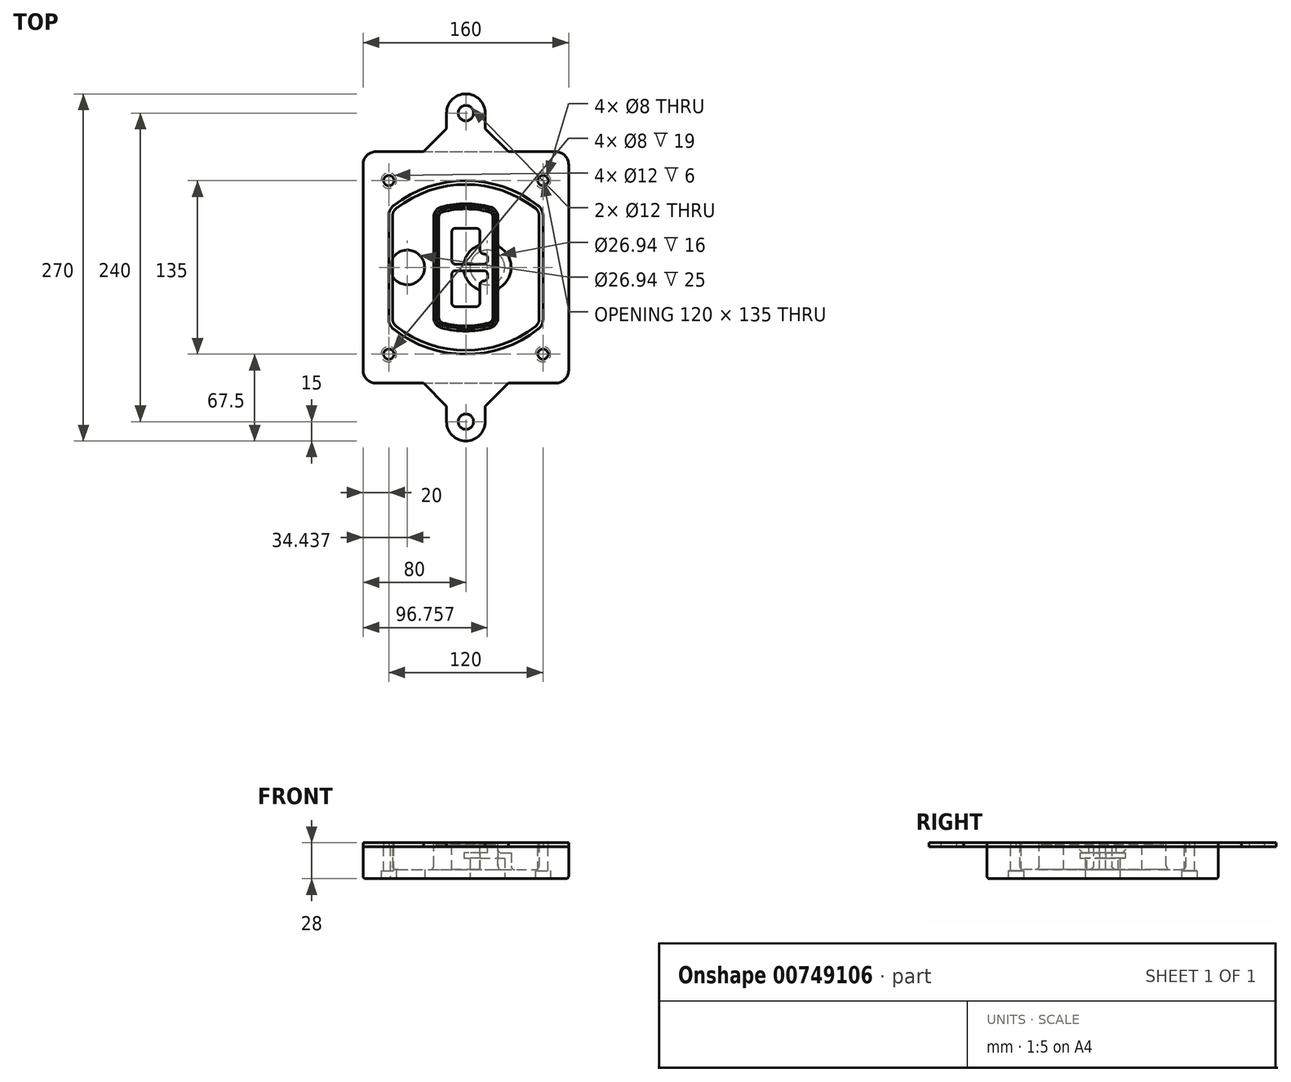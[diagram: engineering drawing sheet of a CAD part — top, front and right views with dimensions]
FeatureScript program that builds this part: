
annotation { "Feature Type Name" : "Feature", "Feature Type Description" : "" }
export const myFeature = defineFeature(function(context is Context, id is Id, definition is map)
    precondition{}
    {
        {
            var Q0;
            Q0=qCreatedBy(makeId("Top.planeOp"),FACE);
            var sketch = newSketch(context, id + "F0", { "sketchPlane" : qUnion([Q0])});
            skPoint(sketch, "E0.rect.middle", {"position": v(0, 0) * mm});
            skLineSegment(sketch, "E1.bottom", {"start": v(-70, -90) * mm, "end": v(70, -90) * mm});
            skLineSegment(sketch, "E1.top", {"start": v(-70, 90) * mm, "end": v(70, 90) * mm});
            skLineSegment(sketch, "E1.left", {"start": v(-80, -80) * mm, "end": v(-80, 80) * mm});
            skLineSegment(sketch, "E1.right", {"start": v(80, -80) * mm, "end": v(80, 80) * mm});
            skLineSegment(sketch, "E2", {"start": v(-80, 90) * mm, "end": v(80, -90) * mm, "construction": true});
            skLineSegment(sketch, "E3", {"start": v(80, 90) * mm, "end": v(-80, -90) * mm, "construction": true});
            skCircle(sketch, "E4", {"center": v(-60, 67.5) * mm, "radius": 4 * mm});
            skCircle(sketch, "E5", {"center": v(60, 67.5) * mm, "radius": 4 * mm});
            skCircle(sketch, "E6", {"center": v(60, -67.5) * mm, "radius": 4 * mm});
            skCircle(sketch, "E7", {"center": v(-60, -67.5) * mm, "radius": 4 * mm});
            skLineSegment(sketch, "E8", {"start": v(-60, 67.5) * mm, "end": v(60, 67.5) * mm, "construction": true});
            skLineSegment(sketch, "E9", {"start": v(60, 67.5) * mm, "end": v(60, -67.5) * mm, "construction": true});
            skLineSegment(sketch, "E10", {"start": v(60, -67.5) * mm, "end": v(-60, -67.5) * mm, "construction": true});
            skLineSegment(sketch, "E11", {"start": v(-60, -67.5) * mm, "end": v(-60, 67.5) * mm, "construction": true});
            skLineSegment(sketch, "E12", {"start": v(-60, 40.3) * mm, "end": v(-60, -40.3) * mm});
            skLineSegment(sketch, "E13", {"start": v(60, 40.3) * mm, "end": v(60, -40.3) * mm});
            skArc(sketch, "E14", {"start": v(56.15, 48.18) * mm, "mid": v(0, 67.5) * mm, "end": v(-56.15, 48.18) * mm});
            skArc(sketch, "E15", {"start": v(-56.15, -48.18) * mm, "mid": v(0, -67.5) * mm, "end": v(56.15, -48.18) * mm});
            skLineSegment(sketch, "E16", {"start": v(-60, 0) * mm, "end": v(60, 0) * mm, "construction": true});
            skPoint(sketch, "E17.visualSharp", {"position": v(-60, -45) * mm});
            skArc(sketch, "E17.filletArc", {"start": v(-60, -40.3) * mm, "mid": v(-58.99, -44.68) * mm, "end": v(-56.15, -48.18) * mm});
            skPoint(sketch, "E18.visualSharp", {"position": v(-60, 45) * mm});
            skArc(sketch, "E18.filletArc", {"start": v(-56.15, 48.18) * mm, "mid": v(-58.99, 44.68) * mm, "end": v(-60, 40.3) * mm});
            skPoint(sketch, "E19.visualSharp", {"position": v(60, 45) * mm});
            skArc(sketch, "E19.filletArc", {"start": v(60, 40.3) * mm, "mid": v(58.99, 44.68) * mm, "end": v(56.15, 48.18) * mm});
            skPoint(sketch, "E20.visualSharp", {"position": v(60, -45) * mm});
            skArc(sketch, "E20.filletArc", {"start": v(56.15, -48.18) * mm, "mid": v(58.99, -44.68) * mm, "end": v(60, -40.3) * mm});
            skPoint(sketch, "E21.visualSharp", {"position": v(-80, 90) * mm});
            skArc(sketch, "E21.filletArc", {"start": v(-70, 90) * mm, "mid": v(-77.07, 87.07) * mm, "end": v(-80, 80) * mm});
            skPoint(sketch, "E22.visualSharp", {"position": v(80, 90) * mm});
            skArc(sketch, "E22.filletArc", {"start": v(80, 80) * mm, "mid": v(77.07, 87.07) * mm, "end": v(70, 90) * mm});
            skPoint(sketch, "E23.visualSharp", {"position": v(80, -90) * mm});
            skArc(sketch, "E23.filletArc", {"start": v(70, -90) * mm, "mid": v(77.07, -87.07) * mm, "end": v(80, -80) * mm});
            skPoint(sketch, "E24.visualSharp", {"position": v(-80, -90) * mm});
            skArc(sketch, "E24.filletArc", {"start": v(-80, -80) * mm, "mid": v(-77.07, -87.07) * mm, "end": v(-70, -90) * mm});
            skArc(sketch, "E25.0", {"start": v(57, 40.3) * mm, "mid": v(56.3, 43.36) * mm, "end": v(54.3, 45.81) * mm});
            skLineSegment(sketch, "E25.1", {"start": v(57, 40.3) * mm, "end": v(57, -40.3) * mm});
            skArc(sketch, "E25.2", {"start": v(54.3, -45.81) * mm, "mid": v(56.3, -43.36) * mm, "end": v(57, -40.3) * mm});
            skArc(sketch, "E25.3", {"start": v(-54.3, -45.81) * mm, "mid": v(0, -64.5) * mm, "end": v(54.3, -45.81) * mm});
            skArc(sketch, "E25.4", {"start": v(-57, -40.3) * mm, "mid": v(-56.3, -43.36) * mm, "end": v(-54.3, -45.81) * mm});
            skArc(sketch, "E25.5", {"start": v(54.3, 45.81) * mm, "mid": v(0, 64.5) * mm, "end": v(-54.3, 45.81) * mm});
            skLineSegment(sketch, "E25.6", {"start": v(-57, 40.3) * mm, "end": v(-57, -40.3) * mm});
            skArc(sketch, "E25.7", {"start": v(-54.3, 45.81) * mm, "mid": v(-56.3, 43.36) * mm, "end": v(-57, 40.3) * mm});
            skArc(sketch, "E26.0", {"start": v(-58.62, 51.33) * mm, "mid": v(-62.58, 46.43) * mm, "end": v(-64, 40.3) * mm});
            skArc(sketch, "E26.1", {"start": v(58.62, 51.33) * mm, "mid": v(0, 71.5) * mm, "end": v(-58.62, 51.33) * mm});
            skArc(sketch, "E26.2", {"start": v(64, 40.3) * mm, "mid": v(62.58, 46.43) * mm, "end": v(58.62, 51.33) * mm});
            skLineSegment(sketch, "E26.3", {"start": v(64, 40.3) * mm, "end": v(64, -40.3) * mm});
            skArc(sketch, "E26.4", {"start": v(58.62, -51.33) * mm, "mid": v(62.58, -46.43) * mm, "end": v(64, -40.3) * mm});
            skLineSegment(sketch, "E26.5", {"start": v(-64, 40.3) * mm, "end": v(-64, -40.3) * mm});
            skArc(sketch, "E26.6", {"start": v(-58.62, -51.33) * mm, "mid": v(0, -71.5) * mm, "end": v(58.62, -51.33) * mm});
            skArc(sketch, "E26.7", {"start": v(-64, -40.3) * mm, "mid": v(-62.58, -46.43) * mm, "end": v(-58.62, -51.33) * mm});
            skSolve(sketch);
        }
        {
            var Q0;
            Q0=makeQuery(id+"F0.imprint","IMPRINT",FACE,{"disambiguationData":[TD([[makeQuery(id+"F0.imprint","IMPRINT",EDGE,{"derivedFrom":sQuery(id+"F0.wireOp",EDGE,"E1.bottom")}),1.0]])]});
            var Q1;
            Q1=makeQuery(id+"F0.imprint","IMPRINT",FACE,{"disambiguationData":[TD([[makeQuery(id+"F0.imprint","IMPRINT",EDGE,{"derivedFrom":sQuery(id+"F0.wireOp",EDGE,"E12")}),1.0]])]});
            var Q2;
            Q2=makeQuery(id+"F0.imprint","IMPRINT",FACE,{"disambiguationData":[TD([[makeQuery(id+"F0.imprint","IMPRINT",EDGE,{"derivedFrom":sQuery(id+"F0.wireOp",EDGE,"E25.0")}),1.0]])]});
            var Q3;
            Q3=makeQuery(id+"F0.imprint","IMPRINT",FACE,{"disambiguationData":[TD([[makeQuery(id+"F0.imprint","IMPRINT",EDGE,{"derivedFrom":sQuery(id+"F0.wireOp",EDGE,"E12")}),-1.0]])]});
            extrude(context, id + "F1", {"entities" : qUnion([Q0, Q1, Q2, Q3]), "oppositeDirection" : true, "depth" : 25 * mm});
        }
        {
            var Q0;
            Q0=makeQuery(id+"F0.imprint","IMPRINT",FACE,{"disambiguationData":[TD([[makeQuery(id+"F0.imprint","IMPRINT",EDGE,{"derivedFrom":sQuery(id+"F0.wireOp",EDGE,"E12")}),1.0]])]});
            extrude(context, id + "F2", {"entities" : qUnion([Q0]), "operationType" : NewBodyOperationType.ADD, "depth" : 3 * mm});
        }
        {
            var Q0;
            Q0=makeQuery(id+"F0.imprint","IMPRINT",FACE,{"disambiguationData":[TD([[makeQuery(id+"F0.imprint","IMPRINT",EDGE,{"derivedFrom":sQuery(id+"F0.wireOp",EDGE,"E25.0")}),1.0]])]});
            extrude(context, id + "F3", {"entities" : qUnion([Q0]), "operationType" : NewBodyOperationType.REMOVE, "oppositeDirection" : true, "depth" : 18 * mm});
        }
        {
            var Q0;
            Q0=makeQuery(id+"F2.opExtrude","CAP_FACE",FACE,{"disambiguationData":[OSD([sQuery(id+"F0.wireOp",EDGE,"E12"),sQuery(id+"F0.wireOp",EDGE,"E13"),sQuery(id+"F0.wireOp",EDGE,"E14"),sQuery(id+"F0.wireOp",EDGE,"E15"),sQuery(id+"F0.wireOp",EDGE,"E17.filletArc"),sQuery(id+"F0.wireOp",EDGE,"E18.filletArc"),sQuery(id+"F0.wireOp",EDGE,"E19.filletArc"),sQuery(id+"F0.wireOp",EDGE,"E20.filletArc"),sQuery(id+"F0.wireOp",EDGE,"E25.0"),sQuery(id+"F0.wireOp",EDGE,"E25.1"),sQuery(id+"F0.wireOp",EDGE,"E25.2"),sQuery(id+"F0.wireOp",EDGE,"E25.3"),sQuery(id+"F0.wireOp",EDGE,"E25.4"),sQuery(id+"F0.wireOp",EDGE,"E25.5"),sQuery(id+"F0.wireOp",EDGE,"E25.6"),sQuery(id+"F0.wireOp",EDGE,"E25.7")])],"isStart":false});
            var sketch = newSketch(context, id + "F4", { "sketchPlane" : qUnion([Q0])});
            skArc(sketch, "E27.0", {"start": v(-19.08, -46.97) * mm, "mid": v(0, -49.5) * mm, "end": v(19.08, -46.97) * mm});
            skArc(sketch, "E28.0", {"start": v(19.08, 46.97) * mm, "mid": v(0, 49.5) * mm, "end": v(-19.08, 46.97) * mm});
            skLineSegment(sketch, "E29", {"start": v(-25, 39.25) * mm, "end": v(-25, -39.25) * mm});
            skLineSegment(sketch, "E30", {"start": v(25, 39.25) * mm, "end": v(25, -39.25) * mm});
            skLineSegment(sketch, "E31", {"start": v(-25, 45.1) * mm, "end": v(25, 45.1) * mm, "construction": true});
            skLineSegment(sketch, "E32", {"start": v(-25, -45.1) * mm, "end": v(25, -45.1) * mm, "construction": true});
            skPoint(sketch, "E33.visualSharp", {"position": v(-25, 45.1) * mm});
            skArc(sketch, "E33.filletArc", {"start": v(-19.08, 46.97) * mm, "mid": v(-23.35, 44.11) * mm, "end": v(-25, 39.25) * mm});
            skPoint(sketch, "E34.visualSharp", {"position": v(25, 45.1) * mm});
            skArc(sketch, "E34.filletArc", {"start": v(25, 39.25) * mm, "mid": v(23.35, 44.11) * mm, "end": v(19.08, 46.97) * mm});
            skPoint(sketch, "E35.visualSharp", {"position": v(25, -45.1) * mm});
            skArc(sketch, "E35.filletArc", {"start": v(19.08, -46.97) * mm, "mid": v(23.35, -44.11) * mm, "end": v(25, -39.25) * mm});
            skPoint(sketch, "E36.visualSharp", {"position": v(-25, -45.1) * mm});
            skArc(sketch, "E36.filletArc", {"start": v(-25, -39.25) * mm, "mid": v(-23.35, -44.11) * mm, "end": v(-19.08, -46.97) * mm});
            skArc(sketch, "E37.0", {"start": v(54.3, 45.81) * mm, "mid": v(0, 64.5) * mm, "end": v(-54.3, 45.81) * mm});
            skArc(sketch, "E37.1", {"start": v(-54.3, 45.81) * mm, "mid": v(-56.3, 43.36) * mm, "end": v(-57, 40.3) * mm});
            skLineSegment(sketch, "E37.2", {"start": v(-57, 40.3) * mm, "end": v(-57, -40.3) * mm});
            skArc(sketch, "E37.3", {"start": v(-57, -40.3) * mm, "mid": v(-56.3, -43.36) * mm, "end": v(-54.3, -45.81) * mm});
            skArc(sketch, "E37.4", {"start": v(-54.3, -45.81) * mm, "mid": v(0, -64.5) * mm, "end": v(54.3, -45.81) * mm});
            skArc(sketch, "E37.5", {"start": v(54.3, -45.81) * mm, "mid": v(56.3, -43.36) * mm, "end": v(57, -40.3) * mm});
            skLineSegment(sketch, "E37.6", {"start": v(57, 40.3) * mm, "end": v(57, -40.3) * mm});
            skArc(sketch, "E37.7", {"start": v(57, 40.3) * mm, "mid": v(56.3, 43.36) * mm, "end": v(54.3, 45.81) * mm});
            skLineSegment(sketch, "E38.0", {"start": v(23, 39.25) * mm, "end": v(23, -39.25) * mm});
            skArc(sketch, "E38.1", {"start": v(18.56, -45.04) * mm, "mid": v(21.76, -42.9) * mm, "end": v(23, -39.25) * mm});
            skArc(sketch, "E38.2", {"start": v(-18.56, -45.04) * mm, "mid": v(0, -47.5) * mm, "end": v(18.56, -45.04) * mm});
            skArc(sketch, "E38.3", {"start": v(-23, -39.25) * mm, "mid": v(-21.76, -42.9) * mm, "end": v(-18.56, -45.04) * mm});
            skLineSegment(sketch, "E38.4", {"start": v(-23, 39.25) * mm, "end": v(-23, -39.25) * mm});
            skArc(sketch, "E38.5", {"start": v(23, 39.25) * mm, "mid": v(21.76, 42.9) * mm, "end": v(18.56, 45.04) * mm});
            skArc(sketch, "E38.6", {"start": v(-18.56, 45.04) * mm, "mid": v(-21.76, 42.9) * mm, "end": v(-23, 39.25) * mm});
            skArc(sketch, "E38.7", {"start": v(18.56, 45.04) * mm, "mid": v(0, 47.5) * mm, "end": v(-18.56, 45.04) * mm});
            skArc(sketch, "E39.0", {"start": v(21, 39.25) * mm, "mid": v(20.18, 41.68) * mm, "end": v(18.04, 43.1) * mm});
            skLineSegment(sketch, "E39.1", {"start": v(21, 39.25) * mm, "end": v(21, -39.25) * mm});
            skArc(sketch, "E39.2", {"start": v(18.04, -43.1) * mm, "mid": v(20.18, -41.68) * mm, "end": v(21, -39.25) * mm});
            skArc(sketch, "E39.3", {"start": v(-18.04, -43.1) * mm, "mid": v(0, -45.5) * mm, "end": v(18.04, -43.1) * mm});
            skArc(sketch, "E39.4", {"start": v(-21, -39.25) * mm, "mid": v(-20.18, -41.68) * mm, "end": v(-18.04, -43.1) * mm});
            skArc(sketch, "E39.5", {"start": v(18.04, 43.1) * mm, "mid": v(0, 45.5) * mm, "end": v(-18.04, 43.1) * mm});
            skLineSegment(sketch, "E39.6", {"start": v(-21, 39.25) * mm, "end": v(-21, -39.25) * mm});
            skArc(sketch, "E39.7", {"start": v(-18.04, 43.1) * mm, "mid": v(-20.18, 41.68) * mm, "end": v(-21, 39.25) * mm});
            skLineSegment(sketch, "E40", {"start": v(-25, 0) * mm, "end": v(25, 0) * mm, "construction": true});
            skLineSegment(sketch, "E41", {"start": v(-11, 5.5) * mm, "end": v(-11, 27.5) * mm});
            skLineSegment(sketch, "E42", {"start": v(-8, 30.5) * mm, "end": v(8, 30.5) * mm});
            skLineSegment(sketch, "E43", {"start": v(11, 27.5) * mm, "end": v(11, 13.5) * mm});
            skLineSegment(sketch, "E44", {"start": v(14, 10.5) * mm, "end": v(14, 10.5) * mm});
            skLineSegment(sketch, "E45", {"start": v(17, 7.5) * mm, "end": v(17, 5.5) * mm});
            skLineSegment(sketch, "E46", {"start": v(14, 2.5) * mm, "end": v(-8, 2.5) * mm});
            skPoint(sketch, "E47.visualSharp", {"position": v(-11, 30.5) * mm});
            skArc(sketch, "E47.filletArc", {"start": v(-8, 30.5) * mm, "mid": v(-10.12, 29.62) * mm, "end": v(-11, 27.5) * mm});
            skPoint(sketch, "E48.visualSharp", {"position": v(11, 30.5) * mm});
            skArc(sketch, "E48.filletArc", {"start": v(11, 27.5) * mm, "mid": v(10.12, 29.62) * mm, "end": v(8, 30.5) * mm});
            skPoint(sketch, "E49.visualSharp", {"position": v(11, 10.5) * mm});
            skArc(sketch, "E49.filletArc", {"start": v(11, 13.5) * mm, "mid": v(11.88, 11.38) * mm, "end": v(14, 10.5) * mm});
            skPoint(sketch, "E50.visualSharp", {"position": v(17, 10.5) * mm});
            skArc(sketch, "E50.filletArc", {"start": v(17, 7.5) * mm, "mid": v(16.12, 9.62) * mm, "end": v(14, 10.5) * mm});
            skPoint(sketch, "E51.visualSharp", {"position": v(17, 2.5) * mm});
            skArc(sketch, "E51.filletArc", {"start": v(14, 2.5) * mm, "mid": v(16.12, 3.38) * mm, "end": v(17, 5.5) * mm});
            skPoint(sketch, "E52.visualSharp", {"position": v(-11, 2.5) * mm});
            skArc(sketch, "E52.filletArc", {"start": v(-11, 5.5) * mm, "mid": v(-10.12, 3.38) * mm, "end": v(-8, 2.5) * mm});
            skLineSegment(sketch, "E53.0.MirrorCS", {"start": v(14, -2.5) * mm, "end": v(-8, -2.5) * mm});
            skArc(sketch, "E54.0.MirrorCS", {"start": v(-11, -5.5) * mm, "mid": v(-10.12, -3.38) * mm, "end": v(-8, -2.5) * mm});
            skLineSegment(sketch, "E55.0.MirrorCS", {"start": v(-11, -5.5) * mm, "end": v(-11, -27.5) * mm});
            skArc(sketch, "E56.0.MirrorCS", {"start": v(-8, -30.5) * mm, "mid": v(-10.12, -29.62) * mm, "end": v(-11, -27.5) * mm});
            skLineSegment(sketch, "E57.0.MirrorCS", {"start": v(-8, -30.5) * mm, "end": v(8, -30.5) * mm});
            skArc(sketch, "E58.0.MirrorCS", {"start": v(11, -27.5) * mm, "mid": v(10.12, -29.62) * mm, "end": v(8, -30.5) * mm});
            skLineSegment(sketch, "E59.0.MirrorCS", {"start": v(11, -27.5) * mm, "end": v(11, -13.5) * mm});
            skArc(sketch, "E60.0.MirrorCS", {"start": v(11, -13.5) * mm, "mid": v(11.88, -11.38) * mm, "end": v(14, -10.5) * mm});
            skArc(sketch, "E61.0.MirrorCS", {"start": v(17, -7.5) * mm, "mid": v(16.12, -9.62) * mm, "end": v(14, -10.5) * mm});
            skLineSegment(sketch, "E62.0.MirrorCS", {"start": v(17, -7.5) * mm, "end": v(17, -5.5) * mm});
            skArc(sketch, "E63.0.MirrorCS", {"start": v(14, -2.5) * mm, "mid": v(16.12, -3.38) * mm, "end": v(17, -5.5) * mm});
            skSolve(sketch);
        }
        {
            var Q0;
            Q0=makeQuery(id+"F4.imprint","IMPRINT",FACE,{"disambiguationData":[TD([[makeQuery(id+"F4.imprint","IMPRINT",EDGE,{"derivedFrom":sQuery(id+"F4.wireOp",EDGE,"E27.0")}),1.0]])]});
            var Q1;
            Q1=makeQuery(id+"F4.imprint","IMPRINT",FACE,{"disambiguationData":[TD([[makeQuery(id+"F4.imprint","IMPRINT",EDGE,{"derivedFrom":sQuery(id+"F4.wireOp",EDGE,"E38.0")}),-1.0]])]});
            var Q2;
            Q2=makeQuery(id+"F4.imprint","IMPRINT",FACE,{"disambiguationData":[TD([[makeQuery(id+"F4.imprint","IMPRINT",EDGE,{"derivedFrom":sQuery(id+"F4.wireOp",EDGE,"E39.0")}),1.0]])]});
            extrude(context, id + "F5", {"entities" : qUnion([Q0, Q1, Q2]), "operationType" : NewBodyOperationType.ADD, "endBound" : BoundingType.UP_TO_NEXT, "oppositeDirection" : true, "depth" : 25 * mm});
        }
        {
            var Q0;
            Q0=makeQuery(id+"F4.imprint","IMPRINT",FACE,{"disambiguationData":[TD([[makeQuery(id+"F4.imprint","IMPRINT",EDGE,{"derivedFrom":sQuery(id+"F4.wireOp",EDGE,"E38.0")}),-1.0]])]});
            extrude(context, id + "F6", {"entities" : qUnion([Q0]), "operationType" : NewBodyOperationType.REMOVE, "oppositeDirection" : true, "depth" : 2 * mm});
        }
        {
            var Q0;
            Q0=makeQuery(id+"F1.opExtrude","CAP_FACE",FACE,{"disambiguationData":[OSD([sQuery(id+"F0.wireOp",EDGE,"E1.bottom"),sQuery(id+"F0.wireOp",EDGE,"E1.top"),sQuery(id+"F0.wireOp",EDGE,"E1.left"),sQuery(id+"F0.wireOp",EDGE,"E1.right"),sQuery(id+"F0.wireOp",EDGE,"E4"),sQuery(id+"F0.wireOp",EDGE,"E5"),sQuery(id+"F0.wireOp",EDGE,"E6"),sQuery(id+"F0.wireOp",EDGE,"E7"),sQuery(id+"F0.wireOp",EDGE,"E21.filletArc"),sQuery(id+"F0.wireOp",EDGE,"E22.filletArc"),sQuery(id+"F0.wireOp",EDGE,"E23.filletArc"),sQuery(id+"F0.wireOp",EDGE,"E24.filletArc")])],"isStart":false});
            var sketch = newSketch(context, id + "F7", { "sketchPlane" : qUnion([Q0])});
            skCircle(sketch, "E64", {"center": v(16.76, 0) * mm, "radius": 13.47 * mm});
            skCircle(sketch, "E65", {"center": v(-45.56, 0) * mm, "radius": 13.47 * mm});
            skLineSegment(sketch, "E66", {"start": v(80, 0) * mm, "end": v(-80, 0) * mm});
            skCircle(sketch, "E67", {"center": v(16.76, 0) * mm, "radius": 18.47 * mm});
            skCircle(sketch, "E68", {"center": v(60, -67.5) * mm, "radius": 6 * mm});
            skCircle(sketch, "E69", {"center": v(-60, -67.5) * mm, "radius": 6 * mm});
            skCircle(sketch, "E70", {"center": v(-60, 67.5) * mm, "radius": 6 * mm});
            skCircle(sketch, "E71", {"center": v(60, 67.5) * mm, "radius": 6 * mm});
            skSolve(sketch);
        }
        {
            var Q0;
            {var subQ1=sQuery(id+"F7.wireOp",EDGE,"E66");var subQ4=sQuery(id+"F7.wireOp",EDGE,"E64");var subQ6=makeQuery(id+"F7.imprint","INTERSECT",VERTEX,{"disambiguationData":[OD(0.0)],"derivedFrom":[subQ4,subQ1]});Q0=makeQuery(id+"F7.imprint","IMPRINT",FACE,{"disambiguationData":[TD([[makeQuery(id+"F7.imprint","IMPRINT",EDGE,{"disambiguationData":[TD([[subQ6,-1.0]])],"derivedFrom":subQ4}),-1.0]])]});}
            var Q1;
            {var subQ0=sQuery(id+"F7.wireOp",EDGE,"E66");var subQ1=sQuery(id+"F7.wireOp",EDGE,"E64");var subQ3=makeQuery(id+"F7.imprint","INTERSECT",VERTEX,{"disambiguationData":[OD(0.0)],"derivedFrom":[subQ1,subQ0]});Q1=makeQuery(id+"F7.imprint","IMPRINT",FACE,{"disambiguationData":[TD([[makeQuery(id+"F7.imprint","IMPRINT",EDGE,{"disambiguationData":[TD([[subQ3,-1.0]])],"derivedFrom":subQ1}),1.0]])]});}
            var Q2;
            {var subQ0=sQuery(id+"F7.wireOp",EDGE,"E66");var subQ1=sQuery(id+"F7.wireOp",EDGE,"E64");var subQ3=makeQuery(id+"F7.imprint","INTERSECT",VERTEX,{"disambiguationData":[OD(0.0)],"derivedFrom":[subQ1,subQ0]});Q2=makeQuery(id+"F7.imprint","IMPRINT",FACE,{"disambiguationData":[TD([[makeQuery(id+"F7.imprint","IMPRINT",EDGE,{"disambiguationData":[TD([[subQ3,1.0]])],"derivedFrom":subQ1}),1.0]])]});}
            var Q3;
            {var subQ1=sQuery(id+"F7.wireOp",EDGE,"E66");var subQ4=sQuery(id+"F7.wireOp",EDGE,"E64");var subQ6=makeQuery(id+"F7.imprint","INTERSECT",VERTEX,{"disambiguationData":[OD(0.0)],"derivedFrom":[subQ4,subQ1]});Q3=makeQuery(id+"F7.imprint","IMPRINT",FACE,{"disambiguationData":[TD([[makeQuery(id+"F7.imprint","IMPRINT",EDGE,{"disambiguationData":[TD([[subQ6,1.0]])],"derivedFrom":subQ4}),-1.0]])]});}
            extrude(context, id + "F8", {"entities" : qUnion([Q0, Q1, Q2, Q3]), "operationType" : NewBodyOperationType.ADD, "oppositeDirection" : true, "depth" : 20 * mm});
        }
        {
            var Q0;
            {var subQ0=sQuery(id+"F7.wireOp",EDGE,"E66");var subQ1=sQuery(id+"F7.wireOp",EDGE,"E64");var subQ3=makeQuery(id+"F7.imprint","INTERSECT",VERTEX,{"disambiguationData":[OD(0.0)],"derivedFrom":[subQ1,subQ0]});Q0=makeQuery(id+"F7.imprint","IMPRINT",FACE,{"disambiguationData":[TD([[makeQuery(id+"F7.imprint","IMPRINT",EDGE,{"disambiguationData":[TD([[subQ3,-1.0]])],"derivedFrom":subQ1}),1.0]])]});}
            var Q1;
            {var subQ0=sQuery(id+"F7.wireOp",EDGE,"E66");var subQ1=sQuery(id+"F7.wireOp",EDGE,"E64");var subQ3=makeQuery(id+"F7.imprint","INTERSECT",VERTEX,{"disambiguationData":[OD(0.0)],"derivedFrom":[subQ1,subQ0]});Q1=makeQuery(id+"F7.imprint","IMPRINT",FACE,{"disambiguationData":[TD([[makeQuery(id+"F7.imprint","IMPRINT",EDGE,{"disambiguationData":[TD([[subQ3,1.0]])],"derivedFrom":subQ1}),1.0]])]});}
            extrude(context, id + "F9", {"entities" : qUnion([Q0, Q1]), "operationType" : NewBodyOperationType.REMOVE, "oppositeDirection" : true, "depth" : 16 * mm});
        }
        {
            var Q0;
            {var subQ0=sQuery(id+"F7.wireOp",EDGE,"E66");var subQ1=sQuery(id+"F7.wireOp",EDGE,"E65");var subQ3=makeQuery(id+"F7.imprint","INTERSECT",VERTEX,{"disambiguationData":[OD(0.0)],"derivedFrom":[subQ1,subQ0]});Q0=makeQuery(id+"F7.imprint","IMPRINT",FACE,{"disambiguationData":[TD([[makeQuery(id+"F7.imprint","IMPRINT",EDGE,{"disambiguationData":[TD([[subQ3,-1.0]])],"derivedFrom":subQ1}),1.0]])]});}
            var Q1;
            {var subQ0=sQuery(id+"F7.wireOp",EDGE,"E66");var subQ1=sQuery(id+"F7.wireOp",EDGE,"E65");var subQ3=makeQuery(id+"F7.imprint","INTERSECT",VERTEX,{"disambiguationData":[OD(0.0)],"derivedFrom":[subQ1,subQ0]});Q1=makeQuery(id+"F7.imprint","IMPRINT",FACE,{"disambiguationData":[TD([[makeQuery(id+"F7.imprint","IMPRINT",EDGE,{"disambiguationData":[TD([[subQ3,1.0]])],"derivedFrom":subQ1}),1.0]])]});}
            extrude(context, id + "F10", {"entities" : qUnion([Q0, Q1]), "operationType" : NewBodyOperationType.REMOVE, "oppositeDirection" : true, "depth" : 25 * mm});
        }
        {
            var Q0;
            Q0=makeQuery(id+"F7.imprint","IMPRINT",FACE,{"disambiguationData":[TD([[makeQuery(id+"F7.imprint","IMPRINT",EDGE,{"derivedFrom":sQuery(id+"F7.wireOp",EDGE,"E68")}),1.0]])]});
            var Q1;
            Q1=makeQuery(id+"F7.imprint","IMPRINT",FACE,{"disambiguationData":[TD([[makeQuery(id+"F7.imprint","IMPRINT",EDGE,{"derivedFrom":makeQuery(id+"F1.opExtrude","CAP_EDGE",EDGE,{"disambiguationData":[OSD([sQuery(id+"F0.wireOp",EDGE,"E5")])],"isStart":false})}),-1.0]])]});
            var Q2;
            Q2=makeQuery(id+"F7.imprint","IMPRINT",FACE,{"disambiguationData":[TD([[makeQuery(id+"F7.imprint","IMPRINT",EDGE,{"derivedFrom":sQuery(id+"F7.wireOp",EDGE,"E69")}),1.0]])]});
            var Q3;
            Q3=makeQuery(id+"F7.imprint","IMPRINT",FACE,{"disambiguationData":[TD([[makeQuery(id+"F7.imprint","IMPRINT",EDGE,{"derivedFrom":makeQuery(id+"F1.opExtrude","CAP_EDGE",EDGE,{"disambiguationData":[OSD([sQuery(id+"F0.wireOp",EDGE,"E4")])],"isStart":false})}),-1.0]])]});
            var Q4;
            Q4=makeQuery(id+"F7.imprint","IMPRINT",FACE,{"disambiguationData":[TD([[makeQuery(id+"F7.imprint","IMPRINT",EDGE,{"derivedFrom":sQuery(id+"F7.wireOp",EDGE,"E70")}),1.0]])]});
            var Q5;
            Q5=makeQuery(id+"F7.imprint","IMPRINT",FACE,{"disambiguationData":[TD([[makeQuery(id+"F7.imprint","IMPRINT",EDGE,{"derivedFrom":makeQuery(id+"F1.opExtrude","CAP_EDGE",EDGE,{"disambiguationData":[OSD([sQuery(id+"F0.wireOp",EDGE,"E7")])],"isStart":false})}),-1.0]])]});
            var Q6;
            Q6=makeQuery(id+"F7.imprint","IMPRINT",FACE,{"disambiguationData":[TD([[makeQuery(id+"F7.imprint","IMPRINT",EDGE,{"derivedFrom":sQuery(id+"F7.wireOp",EDGE,"E71")}),1.0]])]});
            var Q7;
            Q7=makeQuery(id+"F7.imprint","IMPRINT",FACE,{"disambiguationData":[TD([[makeQuery(id+"F7.imprint","IMPRINT",EDGE,{"derivedFrom":makeQuery(id+"F1.opExtrude","CAP_EDGE",EDGE,{"disambiguationData":[OSD([sQuery(id+"F0.wireOp",EDGE,"E6")])],"isStart":false})}),-1.0]])]});
            extrude(context, id + "F11", {"entities" : qUnion([Q0, Q1, Q2, Q3, Q4, Q5, Q6, Q7]), "operationType" : NewBodyOperationType.REMOVE, "oppositeDirection" : true, "depth" : 6 * mm});
        }
        {
            var Q0;
            Q0=makeQuery(id+"F9.boolean.opBoolean","COPY",FACE,{"derivedFrom":makeQuery(id+"F9.opExtrude","CAP_FACE",FACE,{"disambiguationData":[OSD([sQuery(id+"F7.wireOp",EDGE,"E64")])],"isStart":false})});
            var sketch = newSketch(context, id + "F12", { "sketchPlane" : qUnion([Q0])});
            skArc(sketch, "E72.0", {"start": v(11, 17.55) * mm, "mid": v(2.57, 11.82) * mm, "end": v(-1.54, 2.5) * mm});
            skArc(sketch, "E72.1", {"start": v(-1.54, -2.5) * mm, "mid": v(2.57, -11.82) * mm, "end": v(11, -17.55) * mm});
            skLineSegment(sketch, "E73", {"start": v(-1.54, -2.5) * mm, "end": v(14, -2.5) * mm});
            skLineSegment(sketch, "E74.0", {"start": v(14, 2.5) * mm, "end": v(-1.54, 2.5) * mm});
            skArc(sketch, "E74.1", {"start": v(14, 2.5) * mm, "mid": v(16.12, 3.38) * mm, "end": v(17, 5.5) * mm});
            skLineSegment(sketch, "E74.2", {"start": v(17, 7.5) * mm, "end": v(17, 5.5) * mm});
            skArc(sketch, "E74.3", {"start": v(17, 7.5) * mm, "mid": v(16.12, 9.62) * mm, "end": v(14, 10.5) * mm});
            skArc(sketch, "E74.4", {"start": v(11, 13.5) * mm, "mid": v(11.88, 11.38) * mm, "end": v(14, 10.5) * mm});
            skLineSegment(sketch, "E74.5", {"start": v(11, 17.55) * mm, "end": v(11, 13.5) * mm});
            skLineSegment(sketch, "E74.7", {"start": v(14, -2.5) * mm, "end": v(-1.54, -2.5) * mm});
            skArc(sketch, "E74.8", {"start": v(14, -2.5) * mm, "mid": v(16.12, -3.38) * mm, "end": v(17, -5.5) * mm});
            skLineSegment(sketch, "E74.9", {"start": v(17, -7.5) * mm, "end": v(17, -5.5) * mm});
            skArc(sketch, "E74.10", {"start": v(17, -7.5) * mm, "mid": v(16.12, -9.62) * mm, "end": v(14, -10.5) * mm});
            skArc(sketch, "E74.11", {"start": v(11, -13.5) * mm, "mid": v(11.88, -11.38) * mm, "end": v(14, -10.5) * mm});
            skLineSegment(sketch, "E74.12", {"start": v(11, -17.55) * mm, "end": v(11, -13.5) * mm});
            skPoint(sketch, "E75.orphan", {"position": v(11, -27.5) * mm});
            skPoint(sketch, "E76.orphan", {"position": v(-8, -2.5) * mm});
            skPoint(sketch, "E77.orphan", {"position": v(-8, 2.5) * mm});
            skPoint(sketch, "E78.orphan", {"position": v(11, 27.5) * mm});
            skSolve(sketch);
        }
        {
            var Q0;
            {var subQ7=sQuery(id+"F12.wireOp",EDGE,"E72.0");var subQ14=sQuery(id+"F12.wireOp",EDGE,"E72.1");var subQ16=sQuery(id+"F12.wireOp",EDGE,"E74.1");var subQ18=sQuery(id+"F12.wireOp",EDGE,"E74.8");Q0=qUnion([makeQuery(id+"F12.imprint","IMPRINT",FACE,{"disambiguationData":[TD([[makeQuery(id+"F12.imprint","IMPRINT",EDGE,{"derivedFrom":subQ7}),1.0]])]}),makeQuery(id+"F12.imprint","IMPRINT",FACE,{"disambiguationData":[TD([[makeQuery(id+"F12.imprint","IMPRINT",EDGE,{"derivedFrom":subQ14}),1.0]])]}),makeQuery(id+"F12.imprint","IMPRINT",FACE,{"disambiguationData":[TD([[makeQuery(id+"F12.imprint","IMPRINT",EDGE,{"derivedFrom":subQ16}),1.0]])]}),makeQuery(id+"F12.imprint","IMPRINT",FACE,{"disambiguationData":[TD([[makeQuery(id+"F12.imprint","IMPRINT",EDGE,{"derivedFrom":subQ18}),-1.0]])]})]);}
            var Q1;
            Q1=makeQuery(id+"F5.boolean.opBoolean","SPLIT",FACE,{"disambiguationData":[TD([makeQuery(id+"F5.opExtrude","SWEPT_FACE",FACE,{"disambiguationData":[OSD([sQuery(id+"F4.wireOp",EDGE,"E41")])]})])],"derivedFrom":makeQuery(id+"F3.boolean.opBoolean","COPY",FACE,{"derivedFrom":makeQuery(id+"F3.opExtrude","CAP_FACE",FACE,{"disambiguationData":[OSD([sQuery(id+"F0.wireOp",EDGE,"E25.0"),sQuery(id+"F0.wireOp",EDGE,"E25.1"),sQuery(id+"F0.wireOp",EDGE,"E25.2"),sQuery(id+"F0.wireOp",EDGE,"E25.3"),sQuery(id+"F0.wireOp",EDGE,"E25.4"),sQuery(id+"F0.wireOp",EDGE,"E25.5"),sQuery(id+"F0.wireOp",EDGE,"E25.6"),sQuery(id+"F0.wireOp",EDGE,"E25.7")])],"isStart":false})})});
            extrude(context, id + "F13", {"entities" : qUnion([Q0]), "operationType" : NewBodyOperationType.REMOVE, "endBound" : BoundingType.UP_TO_SURFACE, "endBoundEntityFace" : qUnion([Q1]), "depth" : 25 * mm});
        }
        {
            var Q0;
            Q0=makeQuery(id+"F3.boolean.opBoolean","COPY",EDGE,{"derivedFrom":makeQuery(id+"F3.opExtrude","CAP_EDGE",EDGE,{"disambiguationData":[OSD([sQuery(id+"F0.wireOp",EDGE,"E25.6")])],"isStart":false})});
            var Q1;
            Q1=makeQuery(id+"F8.boolean.opBoolean","INTERSECT",EDGE,{"derivedFrom":[makeQuery(id+"F5.opExtrude","SWEPT_FACE",FACE,{"disambiguationData":[OSD([sQuery(id+"F4.wireOp",EDGE,"E30")])]}),makeQuery(id+"F8.opExtrude","CAP_FACE",FACE,{"disambiguationData":[OSD([sQuery(id+"F7.wireOp",EDGE,"E67")])],"isStart":false})]});
            var Q2;
            Q2=makeQuery(id+"F8.boolean.opBoolean","INTERSECT",EDGE,{"disambiguationData":[OD(1.0)],"derivedFrom":[makeQuery(id+"F5.opExtrude","SWEPT_FACE",FACE,{"disambiguationData":[OSD([sQuery(id+"F4.wireOp",EDGE,"E30")])]}),makeQuery(id+"F8.opExtrude","SWEPT_FACE",FACE,{"disambiguationData":[OSD([sQuery(id+"F7.wireOp",EDGE,"E67")])]})]});
            var Q3;
            {var subQ0=sQuery(id+"F4.wireOp",EDGE,"E30");Q3=makeQuery(id+"F8.boolean.opBoolean","SPLIT",EDGE,{"disambiguationData":[TD([makeQuery(id+"F5.opExtrude","SWEPT_FACE",FACE,{"disambiguationData":[OSD([sQuery(id+"F4.wireOp",EDGE,"E35.filletArc")])]})])],"derivedFrom":makeQuery(id+"F5.opExtrude","CAP_EDGE",EDGE,{"disambiguationData":[OSD([subQ0])],"isStart":false})});}
            var Q4;
            {var subQ0=sQuery(id+"F0.wireOp",EDGE,"E25.7");var subQ1=sQuery(id+"F0.wireOp",EDGE,"E25.1");var subQ2=sQuery(id+"F0.wireOp",EDGE,"E25.6");var subQ3=sQuery(id+"F0.wireOp",EDGE,"E25.5");var subQ4=sQuery(id+"F0.wireOp",EDGE,"E25.4");var subQ5=sQuery(id+"F0.wireOp",EDGE,"E25.0");var subQ6=sQuery(id+"F0.wireOp",EDGE,"E25.2");var subQ7=sQuery(id+"F0.wireOp",EDGE,"E25.3");Q4=makeQuery(id+"F8.boolean.opBoolean","INTERSECT",EDGE,{"derivedFrom":[makeQuery(id+"F5.boolean.opBoolean","SPLIT",FACE,{"disambiguationData":[TD([makeQuery(id+"F2.opExtrude","SWEPT_FACE",FACE,{"disambiguationData":[OSD([subQ5])]})])],"derivedFrom":makeQuery(id+"F3.boolean.opBoolean","COPY",FACE,{"derivedFrom":makeQuery(id+"F3.opExtrude","CAP_FACE",FACE,{"disambiguationData":[OSD([subQ5,subQ1,subQ6,subQ7,subQ4,subQ3,subQ2,subQ0])],"isStart":false})})}),makeQuery(id+"F8.opExtrude","SWEPT_FACE",FACE,{"disambiguationData":[OSD([sQuery(id+"F7.wireOp",EDGE,"E67")])]})]});}
            var Q5;
            Q5=makeQuery(id+"F8.boolean.opBoolean","INTERSECT",EDGE,{"disambiguationData":[OD(0.0)],"derivedFrom":[makeQuery(id+"F5.opExtrude","SWEPT_FACE",FACE,{"disambiguationData":[OSD([sQuery(id+"F4.wireOp",EDGE,"E30")])]}),makeQuery(id+"F8.opExtrude","SWEPT_FACE",FACE,{"disambiguationData":[OSD([sQuery(id+"F7.wireOp",EDGE,"E67")])]})]});
            fillet(context, id + "F14", {"entities" : qUnion([Q0, Q1, Q2, Q3, Q4, Q5]), "radius" : 3 * mm, "tangentPropagation" : true, "allowEdgeOverflow" : false});
        }
        {
            var Q0;
            Q0=makeQuery(id+"F1.opExtrude","CAP_EDGE",EDGE,{"disambiguationData":[OSD([sQuery(id+"F0.wireOp",EDGE,"E1.bottom")])],"isStart":false});
            fillet(context, id + "F15", {"entities" : qUnion([Q0]), "radius" : 2 * mm, "tangentPropagation" : true, "allowEdgeOverflow" : false});
        }
        {
            var Q0;
            {var subQ0=sQuery(id+"F0.wireOp",EDGE,"E21.filletArc");var subQ1=sQuery(id+"F0.wireOp",EDGE,"E7");var subQ2=sQuery(id+"F0.wireOp",EDGE,"E6");var subQ3=sQuery(id+"F0.wireOp",EDGE,"E5");var subQ4=sQuery(id+"F0.wireOp",EDGE,"E4");var subQ5=sQuery(id+"F0.wireOp",EDGE,"E22.filletArc");var subQ6=sQuery(id+"F0.wireOp",EDGE,"E1.bottom");var subQ7=sQuery(id+"F0.wireOp",EDGE,"E1.right");var subQ8=sQuery(id+"F0.wireOp",EDGE,"E1.top");var subQ9=sQuery(id+"F0.wireOp",EDGE,"E1.left");var subQ10=sQuery(id+"F0.wireOp",EDGE,"E23.filletArc");var subQ11=sQuery(id+"F0.wireOp",EDGE,"E24.filletArc");Q0=makeQuery(id+"F2.boolean.opBoolean","SPLIT",FACE,{"disambiguationData":[TD([makeQuery(id+"F1.opExtrude","SWEPT_FACE",FACE,{"disambiguationData":[OSD([subQ6])]})])],"derivedFrom":makeQuery(id+"F1.opExtrude","CAP_FACE",FACE,{"disambiguationData":[OSD([subQ6,subQ8,subQ9,subQ7,subQ4,subQ3,subQ2,subQ1,subQ0,subQ5,subQ10,subQ11])],"isStart":true})});}
            var sketch = newSketch(context, id + "F16", { "sketchPlane" : qUnion([Q0])});
            skCircle(sketch, "E79", {"center": v(0, 120) * mm, "radius": 6 * mm});
            skLineSegment(sketch, "E80", {"start": v(0, 120) * mm, "end": v(0, 90) * mm, "construction": true});
            skLineSegment(sketch, "E81", {"start": v(-33, 90) * mm, "end": v(-15, 108) * mm});
            skLineSegment(sketch, "E82", {"start": v(-15, 108) * mm, "end": v(-15, 120) * mm});
            skLineSegment(sketch, "E83.MirrorCS", {"start": v(15, 108) * mm, "end": v(15, 120) * mm});
            skLineSegment(sketch, "E84.MirrorCS", {"start": v(33, 90) * mm, "end": v(15, 108) * mm});
            skArc(sketch, "E85", {"start": v(15, 120) * mm, "mid": v(0, 135) * mm, "end": v(-15, 120) * mm});
            skLineSegment(sketch, "E86", {"start": v(-80, 0) * mm, "end": v(80, 0) * mm, "construction": true});
            skLineSegment(sketch, "E87.MirrorCS", {"start": v(-33, -90) * mm, "end": v(-15, -108) * mm});
            skLineSegment(sketch, "E88.MirrorCS", {"start": v(-15, -108) * mm, "end": v(-15, -120) * mm});
            skArc(sketch, "E89.MirrorCS", {"start": v(15, -120) * mm, "mid": v(0, -135) * mm, "end": v(-15, -120) * mm});
            skLineSegment(sketch, "E90.MirrorCS", {"start": v(15, -108) * mm, "end": v(15, -120) * mm});
            skLineSegment(sketch, "E91.MirrorCS", {"start": v(33, -90) * mm, "end": v(15, -108) * mm});
            skCircle(sketch, "E92.MirrorC", {"center": v(0, -120) * mm, "radius": 6 * mm});
            skLineSegment(sketch, "E93.MirrorCS", {"start": v(0, -120) * mm, "end": v(0, -90) * mm, "construction": true});
            skSolve(sketch);
        }
        {
            var Q0;
            {var subQ0=sQuery(id+"F16.wireOp",EDGE,"E87.MirrorCS");Q0=makeQuery(id+"F16.imprint","IMPRINT",FACE,{"disambiguationData":[TD([[makeQuery(id+"F16.imprint","IMPRINT",EDGE,{"derivedFrom":subQ0}),1.0]])]});}
            var Q1;
            Q1=makeQuery(id+"F16.imprint","IMPRINT",FACE,{"disambiguationData":[TD([[makeQuery(id+"F16.imprint","IMPRINT",EDGE,{"derivedFrom":sQuery(id+"F16.wireOp",EDGE,"E79")}),-1.0]])]});
            var Q2;
            Q2=makeQuery(id+"F16.imprint","IMPRINT",FACE,{"disambiguationData":[TD([[makeQuery(id+"F16.imprint","IMPRINT",EDGE,{"derivedFrom":makeQuery(id+"F1.opExtrude","CAP_EDGE",EDGE,{"disambiguationData":[OSD([sQuery(id+"F0.wireOp",EDGE,"E1.left")])],"isStart":true})}),-1.0]])]});
            var Q3;
            Q3=makeQuery(id+"F2.opExtrude","CAP_FACE",FACE,{"disambiguationData":[OSD([sQuery(id+"F0.wireOp",EDGE,"E12"),sQuery(id+"F0.wireOp",EDGE,"E13"),sQuery(id+"F0.wireOp",EDGE,"E14"),sQuery(id+"F0.wireOp",EDGE,"E15"),sQuery(id+"F0.wireOp",EDGE,"E17.filletArc"),sQuery(id+"F0.wireOp",EDGE,"E18.filletArc"),sQuery(id+"F0.wireOp",EDGE,"E19.filletArc"),sQuery(id+"F0.wireOp",EDGE,"E20.filletArc"),sQuery(id+"F0.wireOp",EDGE,"E25.0"),sQuery(id+"F0.wireOp",EDGE,"E25.1"),sQuery(id+"F0.wireOp",EDGE,"E25.2"),sQuery(id+"F0.wireOp",EDGE,"E25.3"),sQuery(id+"F0.wireOp",EDGE,"E25.4"),sQuery(id+"F0.wireOp",EDGE,"E25.5"),sQuery(id+"F0.wireOp",EDGE,"E25.6"),sQuery(id+"F0.wireOp",EDGE,"E25.7")])],"isStart":false});
            extrude(context, id + "F17", {"entities" : qUnion([Q0, Q1, Q2]), "endBound" : BoundingType.UP_TO_SURFACE, "depth" : 25 * mm, "endBoundEntityFace" : qUnion([Q3]), "offsetDistance" : 25 * mm});
        }
    });
